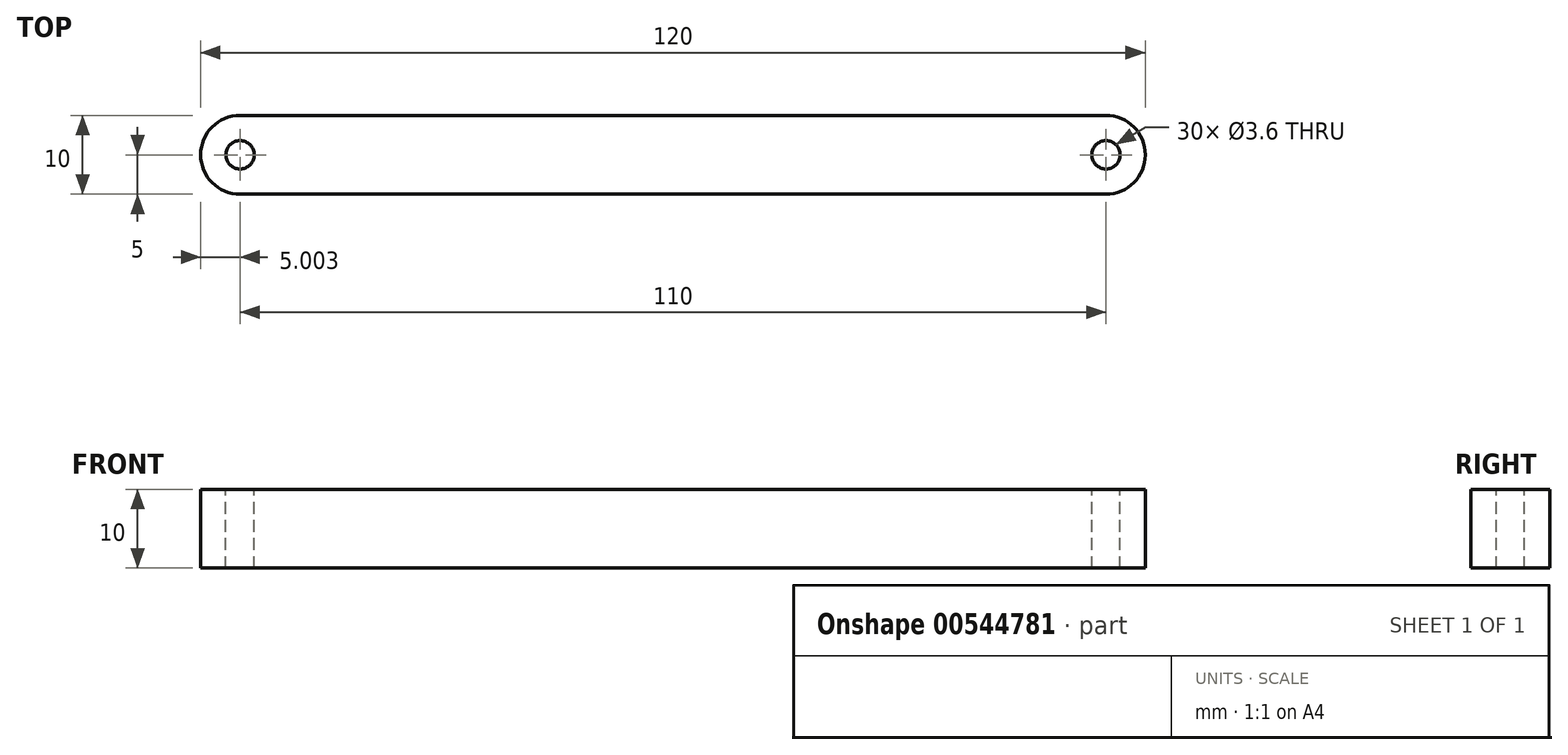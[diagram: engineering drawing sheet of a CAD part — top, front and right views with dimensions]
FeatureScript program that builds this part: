
annotation { "Feature Type Name" : "Feature", "Feature Type Description" : "" }
export const myFeature = defineFeature(function(context is Context, id is Id, definition is map)
    precondition{}
    {
        {
            var Q0;
            Q0=qCreatedBy(makeId("Top.planeOp"),FACE);
            var sketch = newSketch(context, id + "F0", { "sketchPlane" : qUnion([Q0])});
            skLineSegment(sketch, "E0.bottom", {"start": v(13.33, 5) * mm, "end": v(-106.67, 5) * mm});
            skLineSegment(sketch, "E0.top", {"start": v(13.33, -5) * mm, "end": v(-106.67, -5) * mm});
            skPoint(sketch, "E0.middle", {"position": v(0, 0) * mm});
            skPoint(sketch, "E1.visualSharp", {"position": v(-70, 5) * mm});
            skPoint(sketch, "E2.visualSharp", {"position": v(-23.33, -5) * mm});
            skPoint(sketch, "E3.visualSharp", {"position": v(23.33, 5) * mm});
            skPoint(sketch, "E4.visualSharp", {"position": v(70, -5) * mm});
            skLineSegment(sketch, "E5", {"start": v(-106.67, 5) * mm, "end": v(-106.67, -5) * mm});
            skLineSegment(sketch, "E6", {"start": v(13.33, 5) * mm, "end": v(13.33, -5) * mm});
            skSolve(sketch);
        }
        {
            var Q0;
            Q0 = qSketchRegion(id + "F0", true);
            extrude(context, id + "F1", {"entities" : qUnion([Q0]), "endBound" : BoundingType.SYMMETRIC, "depth" : 10 * mm, "offsetDistance" : 25 * mm});
        }
        {
            var Q0;
            Q0=makeQuery(id+"F1.opExtrude","CAP_FACE",FACE,{"disambiguationData":[OSD([sQuery(id+"F0.wireOp",EDGE,"E0.bottom"),sQuery(id+"F0.wireOp",EDGE,"E0.top"),sQuery(id+"F0.wireOp",EDGE,"E0.left"),sQuery(id+"F0.wireOp",EDGE,"E0.right")])],"isStart":false});
            var sketch = newSketch(context, id + "F2", { "sketchPlane" : qUnion([Q0])});
            skCircle(sketch, "E7", {"center": v(55.03, -0.26) * mm, "radius": 1.8 * mm});
            skSolve(sketch);
        }
        {
            var Q0;
            Q0 = qSketchRegion(id + "F2", true);
            extrude(context, id + "F3", {"entities" : qUnion([Q0]), "operationType" : NewBodyOperationType.REMOVE, "oppositeDirection" : true, "depth" : 15 * mm, "offsetDistance" : 25 * mm});
        }
        {
            var Q0;
            Q0=makeQuery(id+"F1.opExtrude","SWEPT_EDGE",EDGE,{"disambiguationData":[OSD([sQuery(id+"F0.wireOp",EDGE,"E0.top"),sQuery(id+"F0.wireOp",EDGE,"E6")])]});
            var Q1;
            Q1=makeQuery(id+"F1.opExtrude","SWEPT_EDGE",EDGE,{"disambiguationData":[OSD([sQuery(id+"F0.wireOp",EDGE,"E0.bottom"),sQuery(id+"F0.wireOp",EDGE,"E6")])]});
            var Q2;
            Q2=makeQuery(id+"F1.opExtrude","SWEPT_EDGE",EDGE,{"disambiguationData":[OSD([sQuery(id+"F0.wireOp",EDGE,"E0.top"),sQuery(id+"F0.wireOp",EDGE,"E5")])]});
            var Q3;
            Q3=makeQuery(id+"F1.opExtrude","SWEPT_EDGE",EDGE,{"disambiguationData":[OSD([sQuery(id+"F0.wireOp",EDGE,"E0.bottom"),sQuery(id+"F0.wireOp",EDGE,"E5")])]});
            fillet(context, id + "F4", {"entities" : qUnion([Q0, Q1, Q2, Q3]), "radius" : 5 * mm, "tangentPropagation" : true, "allowEdgeOverflow" : false});
        }
        {
            var Q0;
            Q0=makeQuery(id+"F1.opExtrude","CAP_FACE",FACE,{"disambiguationData":[OSD([sQuery(id+"F0.wireOp",EDGE,"E0.bottom"),sQuery(id+"F0.wireOp",EDGE,"E0.top"),sQuery(id+"F0.wireOp",EDGE,"E5"),sQuery(id+"F0.wireOp",EDGE,"E6")])],"isStart":false});
            var sketch = newSketch(context, id + "F5", { "sketchPlane" : qUnion([Q0])});
            skCircle(sketch, "E8", {"center": v(-101.67, 0) * mm, "radius": 1.8 * mm});
            skSolve(sketch);
        }
        {
            var Q0;
            Q0 = qSketchRegion(id + "F5", true);
            extrude(context, id + "F6", {"entities" : qUnion([Q0]), "operationType" : NewBodyOperationType.REMOVE, "oppositeDirection" : true, "depth" : 11 * mm, "offsetDistance" : 25 * mm});
        }
        {
            var Q0;
            Q0=makeQuery(id+"F1.opExtrude","CAP_FACE",FACE,{"disambiguationData":[OSD([sQuery(id+"F0.wireOp",EDGE,"E0.bottom"),sQuery(id+"F0.wireOp",EDGE,"E0.top"),sQuery(id+"F0.wireOp",EDGE,"E5"),sQuery(id+"F0.wireOp",EDGE,"E6")])],"isStart":false});
            var sketch = newSketch(context, id + "F7", { "sketchPlane" : qUnion([Q0])});
            skCircle(sketch, "E9", {"center": v(8.33, 0) * mm, "radius": 1.8 * mm});
            skSolve(sketch);
        }
        {
            var Q0;
            Q0 = qSketchRegion(id + "F7", true);
            extrude(context, id + "F8", {"entities" : qUnion([Q0]), "operationType" : NewBodyOperationType.REMOVE, "oppositeDirection" : true, "depth" : 11 * mm, "offsetDistance" : 25 * mm});
        }
    });
